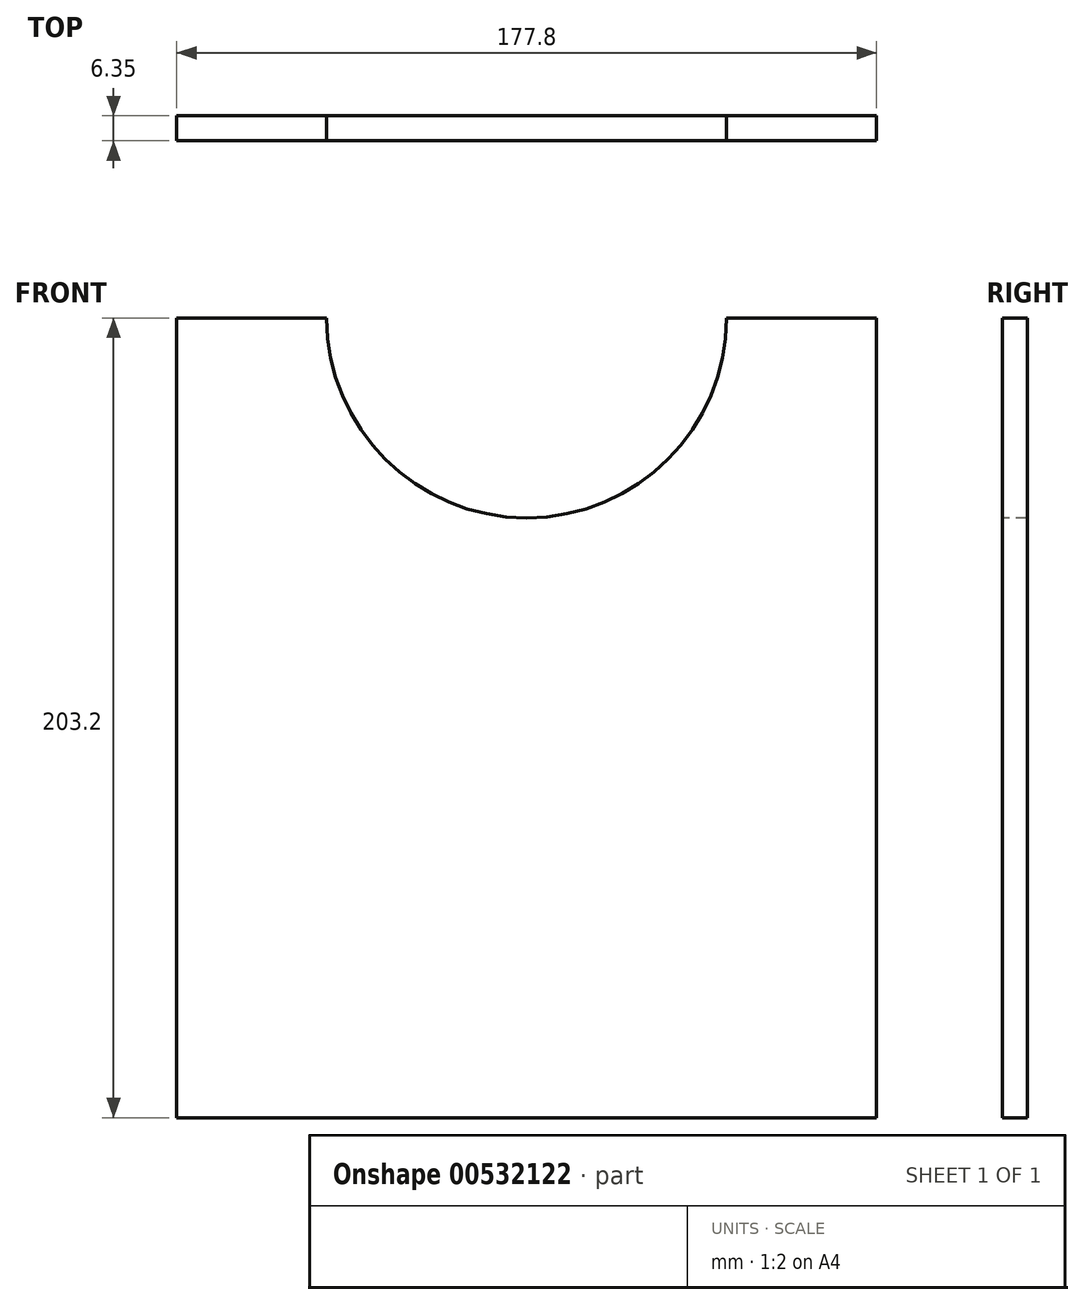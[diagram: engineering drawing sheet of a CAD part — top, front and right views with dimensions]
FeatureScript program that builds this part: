
annotation { "Feature Type Name" : "Feature", "Feature Type Description" : "" }
export const myFeature = defineFeature(function(context is Context, id is Id, definition is map)
    precondition{}
    {
        {
            var Q0;
            Q0=qCreatedBy(makeId("Front.planeOp"),FACE);
            var sketch = newSketch(context, id + "F0", { "sketchPlane" : qUnion([Q0])});
            skLineSegment(sketch, "E0.bottom", {"start": v(88.9, -101.6) * mm, "end": v(-88.9, -101.6) * mm});
            skLineSegment(sketch, "E0.top", {"start": v(88.9, 101.6) * mm, "end": v(-88.9, 101.6) * mm});
            skLineSegment(sketch, "E0.left", {"start": v(88.9, -101.6) * mm, "end": v(88.9, 101.6) * mm});
            skLineSegment(sketch, "E0.right", {"start": v(-88.9, -101.6) * mm, "end": v(-88.9, 101.6) * mm});
            skPoint(sketch, "E0.middle", {"position": v(0, 0) * mm});
            skSolve(sketch);
        }
        {
            var Q0;
            Q0 = qSketchRegion(id + "F0", true);
            extrude(context, id + "F1", {"entities" : qUnion([Q0]), "depth" : 6.35 * mm, "offsetDistance" : 25.4 * mm});
        }
        {
            var Q0;
            Q0=makeQuery(id+"F1.opExtrude","CAP_FACE",FACE,{"disambiguationData":[OSD([sQuery(id+"F0.wireOp",EDGE,"E0.bottom"),sQuery(id+"F0.wireOp",EDGE,"E0.top"),sQuery(id+"F0.wireOp",EDGE,"E0.left"),sQuery(id+"F0.wireOp",EDGE,"E0.right")])],"isStart":false});
            var sketch = newSketch(context, id + "F2", { "sketchPlane" : qUnion([Q0])});
            skArc(sketch, "E1", {"start": v(-50.8, 101.6) * mm, "mid": v(0, 50.8) * mm, "end": v(50.8, 101.6) * mm});
            skSolve(sketch);
        }
        {
            var Q0;
            Q0 = qSketchRegion(id + "F2", true);
            var Q1;
            {var subQ0=sQuery(id+"F2.wireOp",EDGE,"E1");Q1=makeQuery(id+"F2.imprint","IMPRINT",FACE,{"disambiguationData":[TD([[makeQuery(id+"F2.imprint","IMPRINT",EDGE,{"derivedFrom":subQ0}),1.0]])]});}
            extrude(context, id + "F3", {"entities" : qUnion([Q0, Q1]), "operationType" : NewBodyOperationType.REMOVE, "endBound" : BoundingType.THROUGH_ALL, "oppositeDirection" : true, "depth" : 25.4 * mm, "offsetDistance" : 25.4 * mm});
        }
    });
